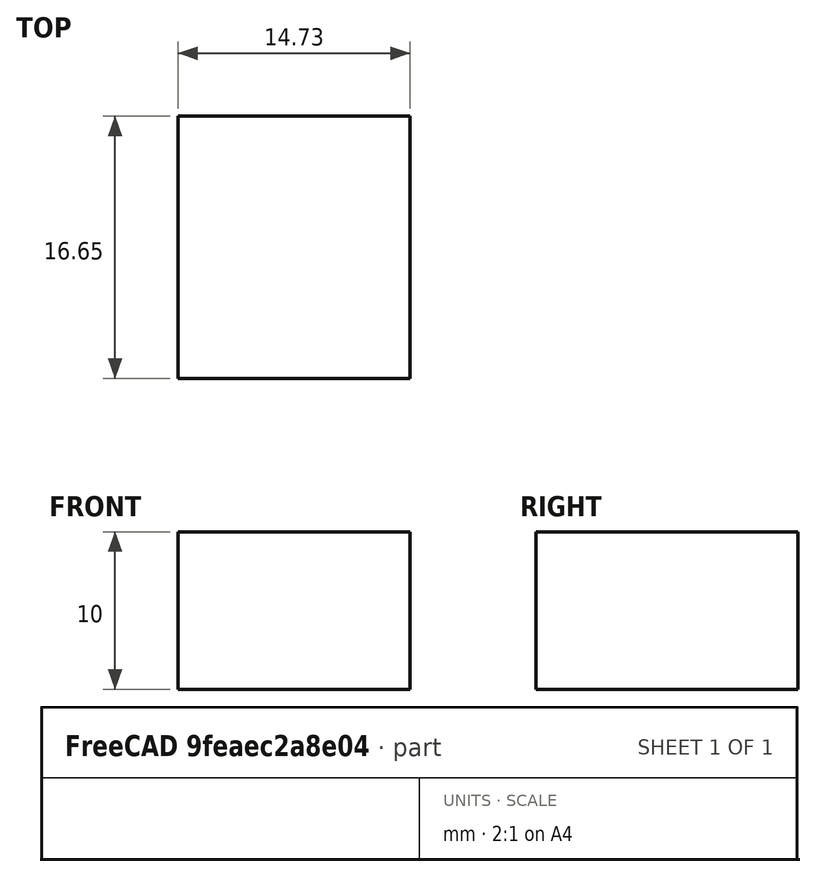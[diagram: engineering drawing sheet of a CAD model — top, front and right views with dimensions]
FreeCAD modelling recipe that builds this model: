
FCSTD DOCUMENT  (FreeCAD 0.20R29603 (Git))
Label: Simple Import
License: All rights reserved
LicenseURL: http://en.wikipedia.org/wiki/All_rights_reserved
objects: Sketcher::SketchObject×1, PartDesign::Pad×1
note: 3 computed .brp shape members not serialized (recipe doc carries the construction recipe); baked Part::Feature solids carry a one-line shape summary decoded from their .brp

FEATURE [Sketcher::SketchObject] Sketch006
  FullyConstrained = false
  MapMode = 5
  Support = -> [XY_Plane001]
  sketch-geometry (4):
    g0: LineSegment StartX=-7.29585 StartY=-8.06207 StartZ=0 EndX=7.42859 EndY=-8.06207 EndZ=0
    g1: LineSegment StartX=7.42859 StartY=-8.06207 StartZ=0 EndX=7.42859 EndY=8.59056 EndZ=0
    g2: LineSegment StartX=7.42859 StartY=8.59056 StartZ=0 EndX=-7.29585 EndY=8.59056 EndZ=0
    g3: LineSegment StartX=-7.29585 StartY=8.59056 StartZ=0 EndX=-7.29585 EndY=-8.06207 EndZ=0
  constraints (8):
    c: Coincident(g0,g1)
    c: Coincident(g1,g2)
    c: Coincident(g2,g3)
    c: Coincident(g3,g0)
    c: Horizontal(g0)
    c: Horizontal(g2)
    c: Vertical(g1)
    c: Vertical(g3)
FEATURE [PartDesign::Pad] Pad001
  Direction = (0,0,1)
  Length = 10
  Length2 = 10
  Profile = -> Sketch006
  ReferenceAxis = -> Sketch006 [N_Axis]
  Type = 0
